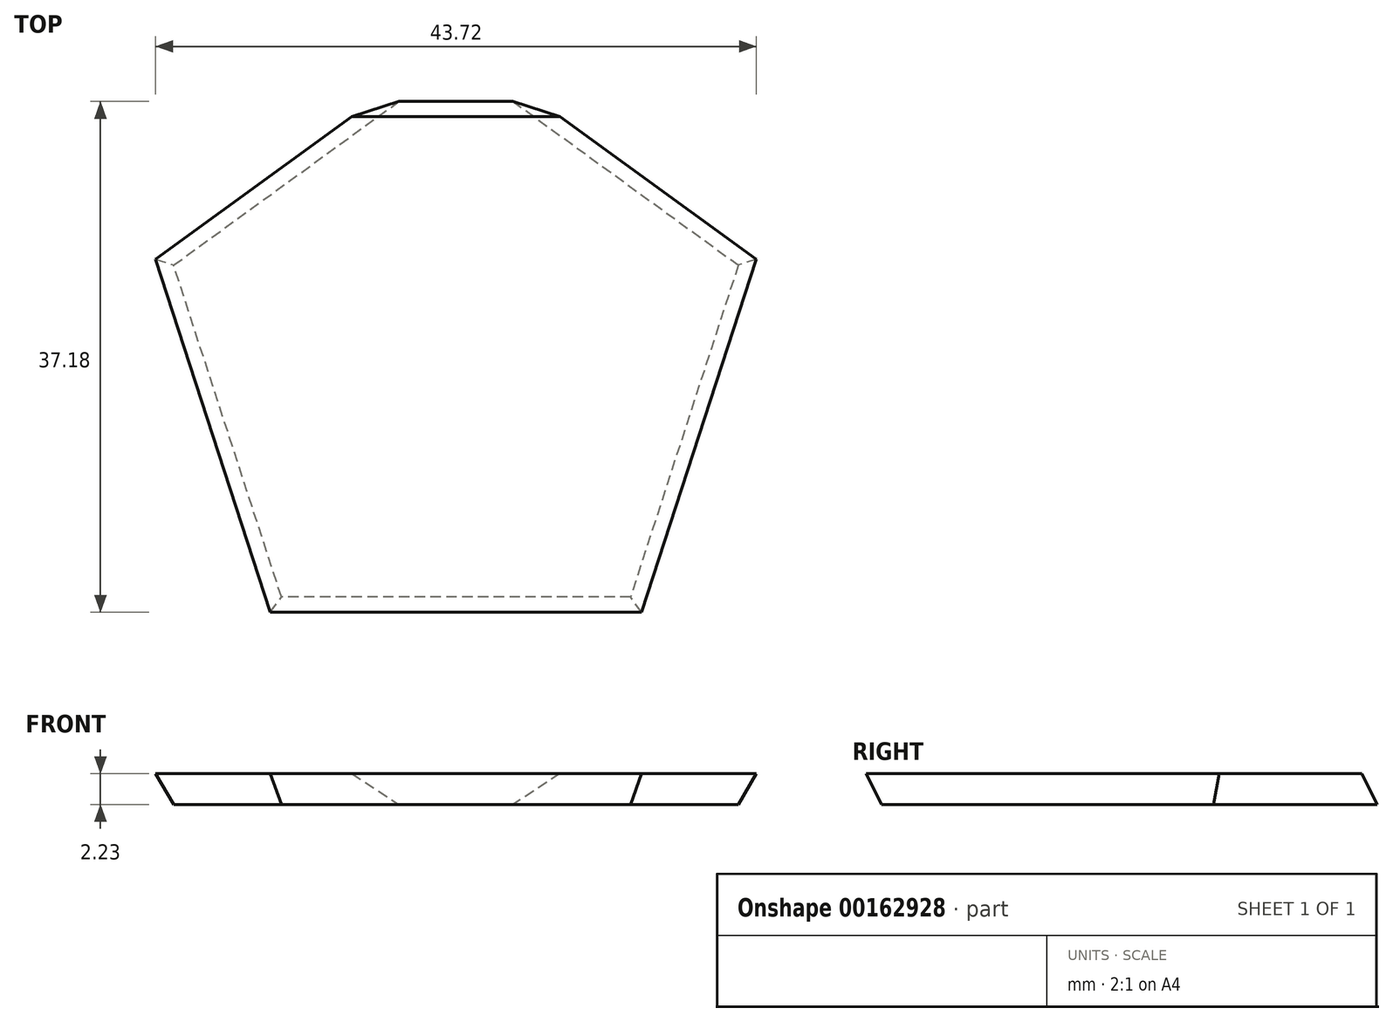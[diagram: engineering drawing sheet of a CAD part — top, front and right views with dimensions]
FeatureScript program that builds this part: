
annotation { "Feature Type Name" : "Feature", "Feature Type Description" : "" }
export const myFeature = defineFeature(function(context is Context, id is Id, definition is map)
    precondition{}
    {
        {
            var Q0;
            Q0=qCreatedBy(makeId("Top.planeOp"),FACE);
            var sketch = newSketch(context, id + "F0", { "sketchPlane" : qUnion([Q0])});
            skCircle(sketch, "E0.cCircle", {"center": v(0, 0) * mm, "radius": 17.48 * mm, "construction": true});
            skLineSegment(sketch, "E0.0", {"start": v(-20.55, 6.68) * mm, "end": v(0, 21.6) * mm});
            skLineSegment(sketch, "E0.1", {"start": v(0, 21.6) * mm, "end": v(20.55, 6.68) * mm});
            skLineSegment(sketch, "E0.2", {"start": v(20.55, 6.68) * mm, "end": v(12.7, -17.48) * mm});
            skLineSegment(sketch, "E0.3", {"start": v(12.7, -17.48) * mm, "end": v(-12.7, -17.48) * mm});
            skLineSegment(sketch, "E0.4", {"start": v(-12.7, -17.48) * mm, "end": v(-20.55, 6.68) * mm});
            skPoint(sketch, "E0.0.midPoint", {"position": v(-10.27, 14.14) * mm});
            skSolve(sketch);
        }
        {
            var Q0;
            Q0 = qSketchRegion(id + "F0", true);
            extrude(context, id + "F1", {"entities" : qUnion([Q0]), "depth" : ((1 / sin(36 * degree)) * (sin(18 * degree) + 1)) * mm, "hasDraft" : true, "draftAngle" : acos(-1 / sqrt(5)) - 90 * degree});
        }
        {
            var Q0;
            Q0=makeQuery(id+"F1.opExtrude","CAP_FACE",FACE,{"disambiguationData":[OSD([sQuery(id+"F0.wireOp",EDGE,"E0.0"),sQuery(id+"F0.wireOp",EDGE,"E0.1"),sQuery(id+"F0.wireOp",EDGE,"E0.2"),sQuery(id+"F0.wireOp",EDGE,"E0.3"),sQuery(id+"F0.wireOp",EDGE,"E0.4")])],"isStart":false});
            var sketch = newSketch(context, id + "F2", { "sketchPlane" : qUnion([Q0])});
            skCircle(sketch, "E1.cCircle", {"center": v(0, 0) * mm, "radius": 17.48 * mm, "construction": true});
            skLineSegment(sketch, "E1.0", {"start": v(-12.7, 17.48) * mm, "end": v(12.7, 17.48) * mm});
            skLineSegment(sketch, "E1.1", {"start": v(12.7, 17.48) * mm, "end": v(20.55, -6.68) * mm});
            skLineSegment(sketch, "E1.2", {"start": v(20.55, -6.68) * mm, "end": v(0, -21.6) * mm});
            skLineSegment(sketch, "E1.3", {"start": v(0, -21.6) * mm, "end": v(-20.55, -6.68) * mm});
            skLineSegment(sketch, "E1.4", {"start": v(-20.55, -6.68) * mm, "end": v(-12.7, 17.48) * mm});
            skPoint(sketch, "E1.0.midPoint", {"position": v(0, 17.48) * mm});
            skSolve(sketch);
        }
        {
            var Q0;
            Q0=makeQuery(id+"F2.imprint","IMPRINT",FACE,{"disambiguationData":[TD([[makeQuery(id+"F2.imprint","IMPRINT",EDGE,{"derivedFrom":sQuery(id+"F2.wireOp",EDGE,"E1.0")}),1.0]])]});
            extrude(context, id + "F3", {"entities" : qUnion([Q0]), "operationType" : NewBodyOperationType.REMOVE, "endBound" : BoundingType.THROUGH_ALL, "oppositeDirection" : true, "depth" : 25.4 * mm, "hasDraft" : true, "draftAngle" : acos(-1 / sqrt(5)) - 90 * degree, "draftPullDirection" : true});
        }
    });
